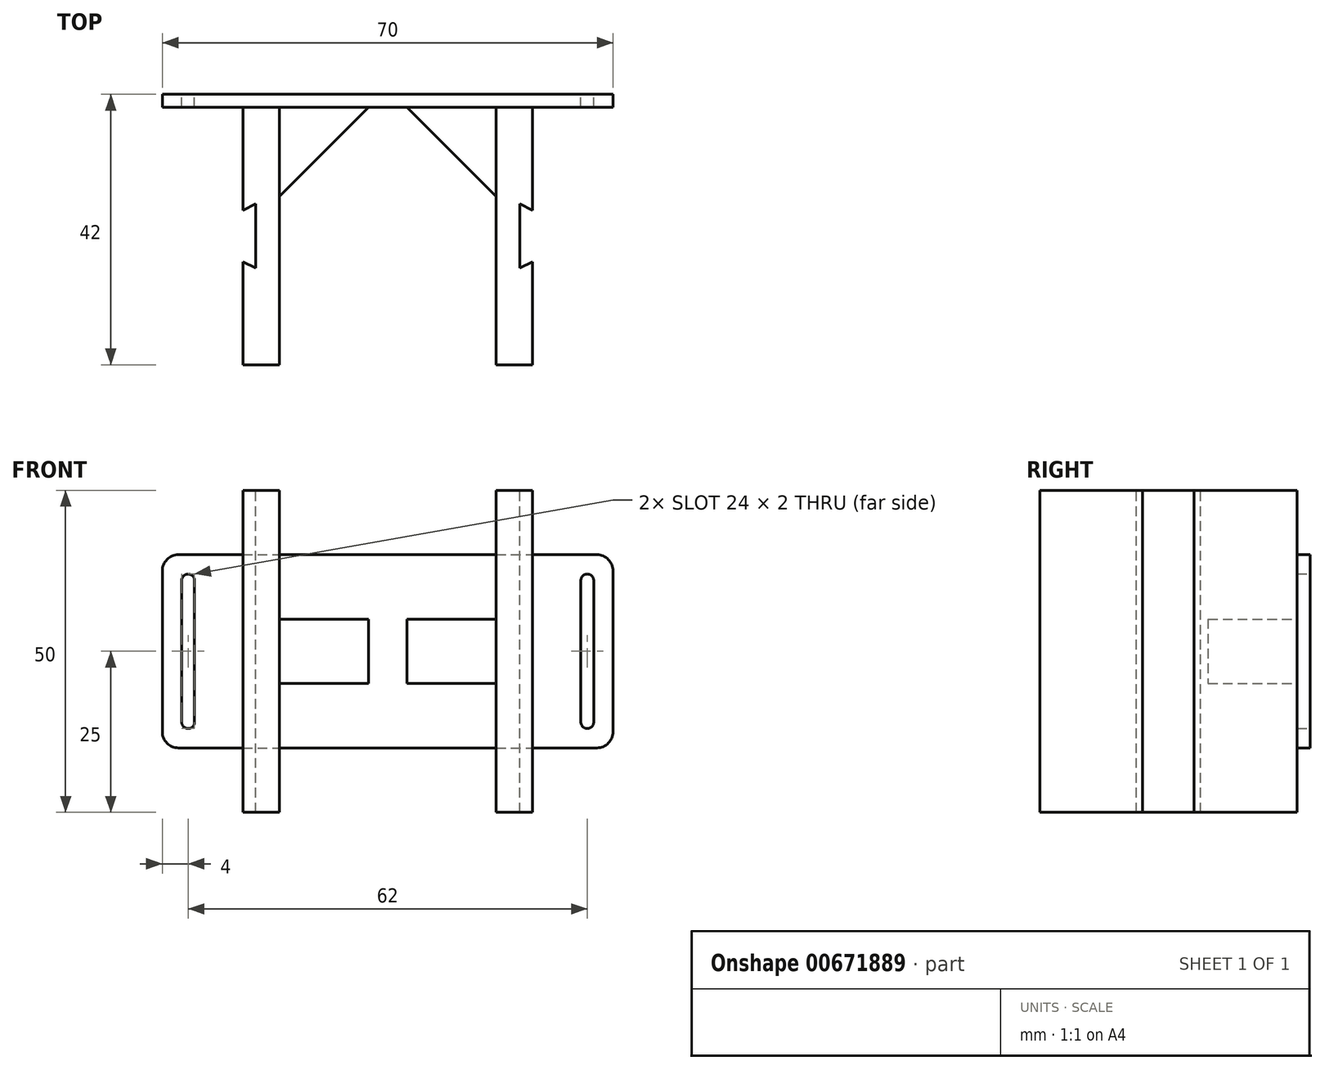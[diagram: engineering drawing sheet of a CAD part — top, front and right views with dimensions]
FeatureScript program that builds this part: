
annotation { "Feature Type Name" : "Feature", "Feature Type Description" : "" }
export const myFeature = defineFeature(function(context is Context, id is Id, definition is map)
    precondition{}
    {
        {
            var Q0;
            Q0=qCreatedBy(makeId("Front.planeOp"),FACE);
            var sketch = newSketch(context, id + "F0", { "sketchPlane" : qUnion([Q0])});
            skLineSegment(sketch, "E0.bottom", {"start": v(-32.5, 15) * mm, "end": v(32.5, 15) * mm});
            skLineSegment(sketch, "E0.top", {"start": v(-32.5, -15) * mm, "end": v(32.5, -15) * mm});
            skLineSegment(sketch, "E0.left", {"start": v(-35, 12.5) * mm, "end": v(-35, -12.5) * mm});
            skLineSegment(sketch, "E0.right", {"start": v(35, 12.5) * mm, "end": v(35, -12.5) * mm});
            skLineSegment(sketch, "E1", {"start": v(-35, 0) * mm, "end": v(35, 0) * mm, "construction": true});
            skLineSegment(sketch, "E2", {"start": v(0, 15) * mm, "end": v(0, -15) * mm, "construction": true});
            skLineSegment(sketch, "E3.bottom", {"start": v(-31, 12) * mm, "end": v(-31, 12) * mm});
            skLineSegment(sketch, "E3.top", {"start": v(-31, -12) * mm, "end": v(-31, -12) * mm});
            skLineSegment(sketch, "E3.left", {"start": v(-32, 11) * mm, "end": v(-32, -11) * mm});
            skLineSegment(sketch, "E3.right", {"start": v(-30, 11) * mm, "end": v(-30, -11) * mm});
            skLineSegment(sketch, "E4.bottom", {"start": v(31, 12) * mm, "end": v(31, 12) * mm});
            skLineSegment(sketch, "E4.top", {"start": v(31, -12) * mm, "end": v(31, -12) * mm});
            skLineSegment(sketch, "E4.left", {"start": v(30, 11) * mm, "end": v(30, -11) * mm});
            skLineSegment(sketch, "E4.right", {"start": v(32, 11) * mm, "end": v(32, -11) * mm});
            skPoint(sketch, "E5.visualSharp", {"position": v(-35, 15) * mm});
            skArc(sketch, "E5.filletArc", {"start": v(-32.5, 15) * mm, "mid": v(-34.27, 14.27) * mm, "end": v(-35, 12.5) * mm});
            skPoint(sketch, "E6.visualSharp", {"position": v(-35, -15) * mm});
            skArc(sketch, "E6.filletArc", {"start": v(-35, -12.5) * mm, "mid": v(-34.27, -14.27) * mm, "end": v(-32.5, -15) * mm});
            skPoint(sketch, "E7.visualSharp", {"position": v(35, -15) * mm});
            skArc(sketch, "E7.filletArc", {"start": v(32.5, -15) * mm, "mid": v(34.27, -14.27) * mm, "end": v(35, -12.5) * mm});
            skPoint(sketch, "E8.visualSharp", {"position": v(35, 15) * mm});
            skArc(sketch, "E8.filletArc", {"start": v(35, 12.5) * mm, "mid": v(34.27, 14.27) * mm, "end": v(32.5, 15) * mm});
            skPoint(sketch, "E9.visualSharp", {"position": v(-30, 12) * mm});
            skArc(sketch, "E9.filletArc", {"start": v(-30, 11) * mm, "mid": v(-30.3, 11.7) * mm, "end": v(-31, 12) * mm});
            skPoint(sketch, "E10.visualSharp", {"position": v(-32, 12) * mm});
            skArc(sketch, "E10.filletArc", {"start": v(-31, 12) * mm, "mid": v(-31.7, 11.7) * mm, "end": v(-32, 11) * mm});
            skPoint(sketch, "E11.visualSharp", {"position": v(-32, -12) * mm});
            skArc(sketch, "E11.filletArc", {"start": v(-32, -11) * mm, "mid": v(-31.7, -11.7) * mm, "end": v(-31, -12) * mm});
            skPoint(sketch, "E12.visualSharp", {"position": v(-30, -12) * mm});
            skArc(sketch, "E12.filletArc", {"start": v(-31, -12) * mm, "mid": v(-30.3, -11.7) * mm, "end": v(-30, -11) * mm});
            skPoint(sketch, "E13.visualSharp", {"position": v(30, 12) * mm});
            skArc(sketch, "E13.filletArc", {"start": v(31, 12) * mm, "mid": v(30.3, 11.7) * mm, "end": v(30, 11) * mm});
            skPoint(sketch, "E14.visualSharp", {"position": v(32, 12) * mm});
            skArc(sketch, "E14.filletArc", {"start": v(32, 11) * mm, "mid": v(31.7, 11.7) * mm, "end": v(31, 12) * mm});
            skPoint(sketch, "E15.visualSharp", {"position": v(30, -12) * mm});
            skArc(sketch, "E15.filletArc", {"start": v(30, -11) * mm, "mid": v(30.3, -11.7) * mm, "end": v(31, -12) * mm});
            skPoint(sketch, "E16.visualSharp", {"position": v(32, -12) * mm});
            skArc(sketch, "E16.filletArc", {"start": v(31, -12) * mm, "mid": v(31.7, -11.7) * mm, "end": v(32, -11) * mm});
            skSolve(sketch);
        }
        {
            var Q0;
            Q0=makeQuery(id+"F0.imprint","IMPRINT",FACE,{"disambiguationData":[TD([[makeQuery(id+"F0.imprint","IMPRINT",EDGE,{"derivedFrom":sQuery(id+"F0.wireOp",EDGE,"E0.bottom")}),-1.0]])]});
            extrude(context, id + "F1", {"entities" : qUnion([Q0]), "depth" : 2 * mm, "offsetDistance" : 25 * mm});
        }
        {
            var Q0;
            Q0=makeQuery(id+"F1.opExtrude","CAP_FACE",FACE,{"disambiguationData":[OSD([sQuery(id+"F0.wireOp",EDGE,"E0.bottom"),sQuery(id+"F0.wireOp",EDGE,"E0.top"),sQuery(id+"F0.wireOp",EDGE,"E0.left"),sQuery(id+"F0.wireOp",EDGE,"E0.right"),sQuery(id+"F0.wireOp",EDGE,"E3.left"),sQuery(id+"F0.wireOp",EDGE,"E3.right"),sQuery(id+"F0.wireOp",EDGE,"E4.left"),sQuery(id+"F0.wireOp",EDGE,"E4.right"),sQuery(id+"F0.wireOp",EDGE,"E5.filletArc"),sQuery(id+"F0.wireOp",EDGE,"E6.filletArc"),sQuery(id+"F0.wireOp",EDGE,"E7.filletArc"),sQuery(id+"F0.wireOp",EDGE,"E8.filletArc"),sQuery(id+"F0.wireOp",EDGE,"E9.filletArc"),sQuery(id+"F0.wireOp",EDGE,"E10.filletArc"),sQuery(id+"F0.wireOp",EDGE,"E11.filletArc"),sQuery(id+"F0.wireOp",EDGE,"E12.filletArc"),sQuery(id+"F0.wireOp",EDGE,"E13.filletArc"),sQuery(id+"F0.wireOp",EDGE,"E14.filletArc"),sQuery(id+"F0.wireOp",EDGE,"E15.filletArc"),sQuery(id+"F0.wireOp",EDGE,"E16.filletArc")])],"isStart":false});
            var sketch = newSketch(context, id + "F2", { "sketchPlane" : qUnion([Q0])});
            skLineSegment(sketch, "E17.bottom", {"start": v(-22.5, 25) * mm, "end": v(-16.85, 25) * mm});
            skLineSegment(sketch, "E17.top", {"start": v(-22.5, -25) * mm, "end": v(-16.85, -25) * mm});
            skLineSegment(sketch, "E17.left", {"start": v(-22.5, 25) * mm, "end": v(-22.5, -25) * mm});
            skLineSegment(sketch, "E17.right", {"start": v(-16.85, 25) * mm, "end": v(-16.85, -25) * mm});
            skLineSegment(sketch, "E18.bottom", {"start": v(16.85, 25) * mm, "end": v(22.5, 25) * mm});
            skLineSegment(sketch, "E18.top", {"start": v(16.85, -25) * mm, "end": v(22.5, -25) * mm});
            skLineSegment(sketch, "E18.left", {"start": v(16.85, 25) * mm, "end": v(16.85, -25) * mm});
            skLineSegment(sketch, "E18.right", {"start": v(22.5, 25) * mm, "end": v(22.5, -25) * mm});
            skLineSegment(sketch, "E19", {"start": v(-22.5, 0) * mm, "end": v(-16.85, 0) * mm, "construction": true});
            skLineSegment(sketch, "E20", {"start": v(16.85, 0) * mm, "end": v(22.5, 0) * mm, "construction": true});
            skLineSegment(sketch, "E21", {"start": v(-35, 0) * mm, "end": v(35, 0) * mm, "construction": true});
            skLineSegment(sketch, "E22", {"start": v(-16.85, 0) * mm, "end": v(16.85, 0) * mm, "construction": true});
            skSolve(sketch);
        }
        {
            var Q0;
            {var subQ0=sQuery(id+"F2.wireOp",EDGE,"E17.bottom");Q0=makeQuery(id+"F2.imprint","IMPRINT",FACE,{"disambiguationData":[TD([[makeQuery(id+"F2.imprint","IMPRINT",EDGE,{"derivedFrom":subQ0}),-1.0]])]});}
            var Q1;
            {var subQ0=sQuery(id+"F2.wireOp",EDGE,"E17.left");var subQ1=makeQuery(id+"F1.opExtrude","CAP_EDGE",EDGE,{"disambiguationData":[OSD([sQuery(id+"F0.wireOp",EDGE,"E0.bottom")])],"isStart":false});var subQ2=makeQuery(id+"F2.imprint","INTERSECT",VERTEX,{"derivedFrom":[subQ1,subQ0]});Q1=makeQuery(id+"F2.imprint","IMPRINT",FACE,{"disambiguationData":[TD([[makeQuery(id+"F2.imprint","IMPRINT",EDGE,{"disambiguationData":[TD([[subQ2,-1.0]])],"derivedFrom":subQ0}),1.0]])]});}
            var Q2;
            {var subQ0=sQuery(id+"F2.wireOp",EDGE,"E17.top");Q2=makeQuery(id+"F2.imprint","IMPRINT",FACE,{"disambiguationData":[TD([[makeQuery(id+"F2.imprint","IMPRINT",EDGE,{"derivedFrom":subQ0}),1.0]])]});}
            var Q3;
            {var subQ0=sQuery(id+"F2.wireOp",EDGE,"E18.top");Q3=makeQuery(id+"F2.imprint","IMPRINT",FACE,{"disambiguationData":[TD([[makeQuery(id+"F2.imprint","IMPRINT",EDGE,{"derivedFrom":subQ0}),1.0]])]});}
            var Q4;
            {var subQ0=sQuery(id+"F2.wireOp",EDGE,"E18.left");var subQ1=makeQuery(id+"F1.opExtrude","CAP_EDGE",EDGE,{"disambiguationData":[OSD([sQuery(id+"F0.wireOp",EDGE,"E0.bottom")])],"isStart":false});var subQ2=makeQuery(id+"F2.imprint","INTERSECT",VERTEX,{"derivedFrom":[subQ1,subQ0]});Q4=makeQuery(id+"F2.imprint","IMPRINT",FACE,{"disambiguationData":[TD([[makeQuery(id+"F2.imprint","IMPRINT",EDGE,{"disambiguationData":[TD([[subQ2,-1.0]])],"derivedFrom":subQ0}),1.0]])]});}
            var Q5;
            {var subQ0=sQuery(id+"F2.wireOp",EDGE,"E18.bottom");Q5=makeQuery(id+"F2.imprint","IMPRINT",FACE,{"disambiguationData":[TD([[makeQuery(id+"F2.imprint","IMPRINT",EDGE,{"derivedFrom":subQ0}),-1.0]])]});}
            extrude(context, id + "F3", {"entities" : qUnion([Q0, Q1, Q2, Q3, Q4, Q5]), "operationType" : NewBodyOperationType.ADD, "depth" : 40 * mm, "offsetDistance" : 25 * mm});
        }
        {
            var Q0;
            Q0=makeQuery(id+"F3.opExtrude","SWEPT_FACE",FACE,{"disambiguationData":[OSD([sQuery(id+"F2.wireOp",EDGE,"E17.bottom")])]});
            var sketch = newSketch(context, id + "F4", { "sketchPlane" : qUnion([Q0])});
            skLineSegment(sketch, "E23.left", {"start": v(-22.5, -18) * mm, "end": v(-22.5, -26) * mm});
            skLineSegment(sketch, "E23.right", {"start": v(-20.5, -18) * mm, "end": v(-20.5, -26) * mm});
            skLineSegment(sketch, "E24", {"start": v(-20.5, -26) * mm, "end": v(-20.5, -27) * mm});
            skLineSegment(sketch, "E25", {"start": v(-22.5, -26) * mm, "end": v(-20.5, -27) * mm});
            skLineSegment(sketch, "E26", {"start": v(-20.5, -18) * mm, "end": v(-20.5, -17) * mm});
            skLineSegment(sketch, "E27", {"start": v(-22.5, -18) * mm, "end": v(-20.5, -17) * mm});
            skLineSegment(sketch, "E28", {"start": v(-16.85, -22) * mm, "end": v(-22.5, -22) * mm, "construction": true});
            skSolve(sketch);
        }
        {
            var Q0;
            Q0=makeQuery(id+"F4.imprint","IMPRINT",FACE,{"disambiguationData":[TD([[makeQuery(id+"F4.imprint","IMPRINT",EDGE,{"derivedFrom":sQuery(id+"F4.wireOp",EDGE,"E23.left")}),-1.0]])]});
            extrude(context, id + "F5", {"entities" : qUnion([Q0]), "operationType" : NewBodyOperationType.REMOVE, "endBound" : BoundingType.UP_TO_NEXT, "oppositeDirection" : true, "depth" : 25 * mm, "offsetDistance" : 25 * mm});
        }
        {
            var Q0;
            Q0=makeQuery(id+"F3.opExtrude","SWEPT_FACE",FACE,{"disambiguationData":[OSD([sQuery(id+"F2.wireOp",EDGE,"E18.bottom")])]});
            var sketch = newSketch(context, id + "F6", { "sketchPlane" : qUnion([Q0])});
            skLineSegment(sketch, "E29.left", {"start": v(22.5, -18) * mm, "end": v(22.5, -26) * mm});
            skLineSegment(sketch, "E29.right", {"start": v(20.5, -18) * mm, "end": v(20.5, -26) * mm});
            skLineSegment(sketch, "E30", {"start": v(20.5, -18) * mm, "end": v(20.5, -17) * mm});
            skLineSegment(sketch, "E31", {"start": v(22.5, -18) * mm, "end": v(20.5, -17) * mm});
            skLineSegment(sketch, "E32", {"start": v(20.5, -26) * mm, "end": v(20.5, -27) * mm});
            skLineSegment(sketch, "E33", {"start": v(20.5, -27) * mm, "end": v(22.5, -26) * mm});
            skLineSegment(sketch, "E34", {"start": v(16.85, -22) * mm, "end": v(22.5, -22) * mm, "construction": true});
            skSolve(sketch);
        }
        {
            var Q0;
            Q0=makeQuery(id+"F6.imprint","IMPRINT",FACE,{"disambiguationData":[TD([[makeQuery(id+"F6.imprint","IMPRINT",EDGE,{"derivedFrom":sQuery(id+"F6.wireOp",EDGE,"E29.left")}),1.0]])]});
            extrude(context, id + "F7", {"entities" : qUnion([Q0]), "operationType" : NewBodyOperationType.REMOVE, "endBound" : BoundingType.UP_TO_NEXT, "oppositeDirection" : true, "depth" : 25 * mm, "offsetDistance" : 25 * mm});
        }
        {
            var Q0;
            {var subQ0=sQuery(id+"F2.wireOp",EDGE,"E17.right");var subQ1=sQuery(id+"F0.wireOp",EDGE,"E0.top");var subQ2=sQuery(id+"F0.wireOp",EDGE,"E0.bottom");Q0=makeQuery(id+"F3.boolean.opBoolean","SPLIT",FACE,{"disambiguationData":[TD([makeQuery(id+"F3.opExtrude","SWEPT_FACE",FACE,{"disambiguationData":[OSD([subQ0])]})])],"derivedFrom":makeQuery(id+"F1.opExtrude","CAP_FACE",FACE,{"disambiguationData":[OSD([subQ2,subQ1,sQuery(id+"F0.wireOp",EDGE,"E0.left"),sQuery(id+"F0.wireOp",EDGE,"E0.right"),sQuery(id+"F0.wireOp",EDGE,"E3.left"),sQuery(id+"F0.wireOp",EDGE,"E3.right"),sQuery(id+"F0.wireOp",EDGE,"E4.left"),sQuery(id+"F0.wireOp",EDGE,"E4.right"),sQuery(id+"F0.wireOp",EDGE,"E5.filletArc"),sQuery(id+"F0.wireOp",EDGE,"E6.filletArc"),sQuery(id+"F0.wireOp",EDGE,"E7.filletArc"),sQuery(id+"F0.wireOp",EDGE,"E8.filletArc"),sQuery(id+"F0.wireOp",EDGE,"E9.filletArc"),sQuery(id+"F0.wireOp",EDGE,"E10.filletArc"),sQuery(id+"F0.wireOp",EDGE,"E11.filletArc"),sQuery(id+"F0.wireOp",EDGE,"E12.filletArc"),sQuery(id+"F0.wireOp",EDGE,"E13.filletArc"),sQuery(id+"F0.wireOp",EDGE,"E14.filletArc"),sQuery(id+"F0.wireOp",EDGE,"E15.filletArc"),sQuery(id+"F0.wireOp",EDGE,"E16.filletArc")])],"isStart":false})});}
            var sketch = newSketch(context, id + "F8", { "sketchPlane" : qUnion([Q0])});
            skLineSegment(sketch, "E35.bottom", {"start": v(-16.85, 5) * mm, "end": v(-3, 5) * mm});
            skLineSegment(sketch, "E35.top", {"start": v(-16.85, -5) * mm, "end": v(-3, -5) * mm});
            skLineSegment(sketch, "E35.left", {"start": v(-16.85, 5) * mm, "end": v(-16.85, -5) * mm});
            skLineSegment(sketch, "E35.right", {"start": v(-3, 5) * mm, "end": v(-3, -5) * mm});
            skLineSegment(sketch, "E36.bottom", {"start": v(16.85, 5) * mm, "end": v(3, 5) * mm});
            skLineSegment(sketch, "E36.top", {"start": v(16.85, -5) * mm, "end": v(3, -5) * mm});
            skLineSegment(sketch, "E36.left", {"start": v(16.85, 5) * mm, "end": v(16.85, -5) * mm});
            skLineSegment(sketch, "E36.right", {"start": v(3, 5) * mm, "end": v(3, -5) * mm});
            skLineSegment(sketch, "E37", {"start": v(0, 0) * mm, "end": v(-3, 0) * mm, "construction": true});
            skLineSegment(sketch, "E38", {"start": v(0, 0) * mm, "end": v(3, 0) * mm, "construction": true});
            skSolve(sketch);
        }
        {
            var Q0;
            Q0=makeQuery(id+"F8.imprint","IMPRINT",FACE,{"disambiguationData":[TD([[makeQuery(id+"F8.imprint","IMPRINT",EDGE,{"derivedFrom":sQuery(id+"F8.wireOp",EDGE,"E35.bottom")}),-1.0]])]});
            var Q1;
            Q1=makeQuery(id+"F8.imprint","IMPRINT",FACE,{"disambiguationData":[TD([[makeQuery(id+"F8.imprint","IMPRINT",EDGE,{"derivedFrom":sQuery(id+"F8.wireOp",EDGE,"E36.bottom")}),1.0]])]});
            extrude(context, id + "F9", {"entities" : qUnion([Q0, Q1]), "operationType" : NewBodyOperationType.ADD, "depth" : 15 * mm, "offsetDistance" : 25 * mm});
        }
        {
            var Q0;
            Q0=makeQuery(id+"F9.opExtrude","CAP_EDGE",EDGE,{"disambiguationData":[OSD([sQuery(id+"F8.wireOp",EDGE,"E35.right")])],"isStart":false});
            var Q1;
            Q1=makeQuery(id+"F9.opExtrude","CAP_EDGE",EDGE,{"disambiguationData":[OSD([sQuery(id+"F8.wireOp",EDGE,"E36.right")])],"isStart":false});
            chamfer(context, id + "F10", {"entities" : qUnion([Q0, Q1]), "width" : 15 * mm, "tangentPropagation" : true});
        }
    });
